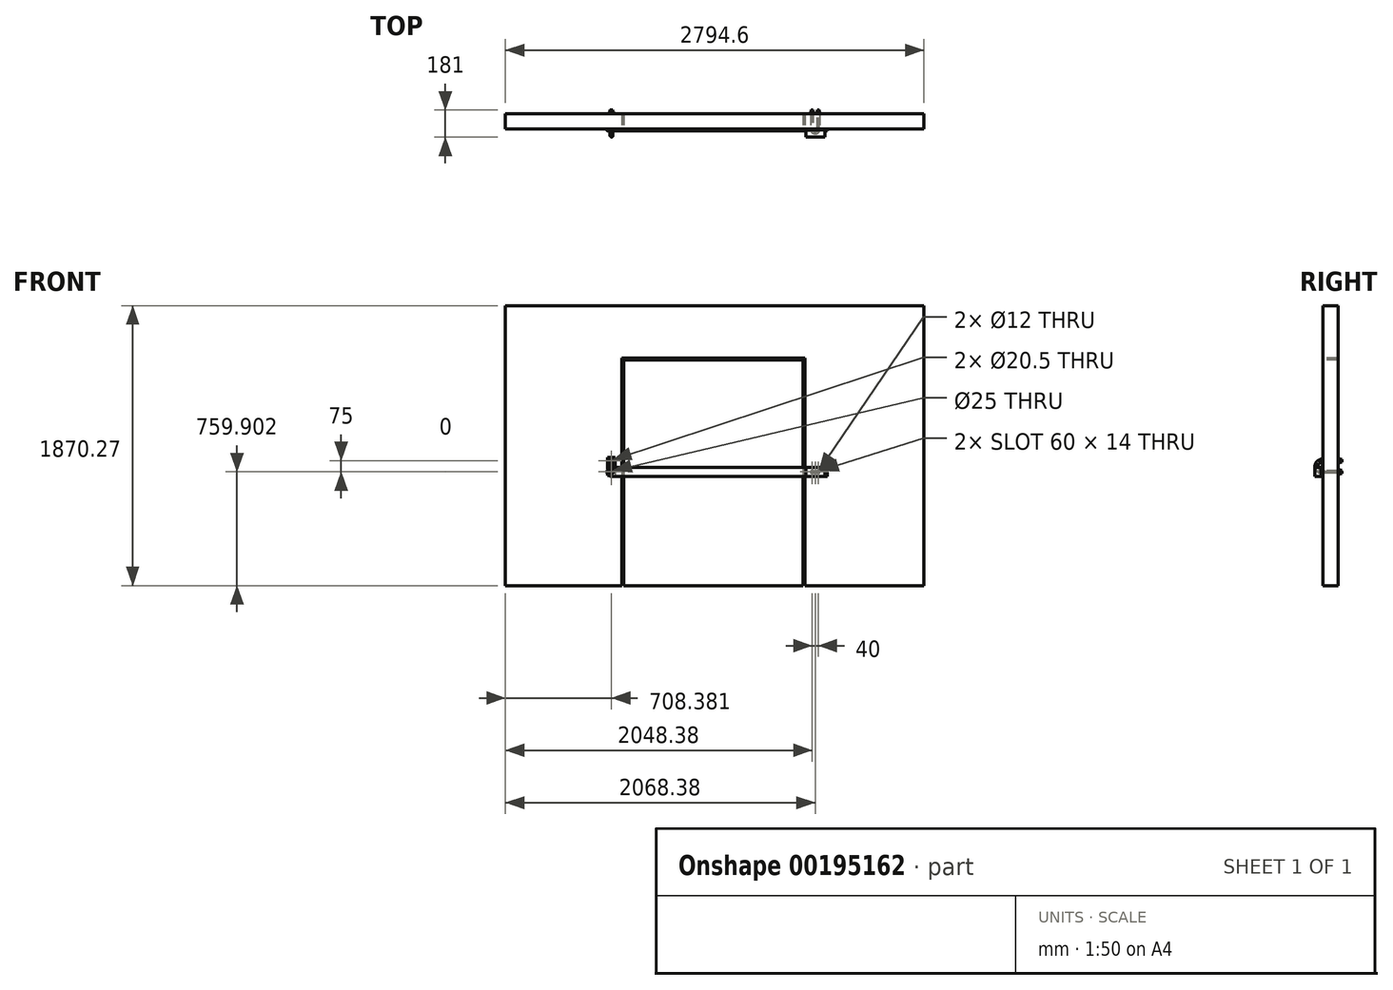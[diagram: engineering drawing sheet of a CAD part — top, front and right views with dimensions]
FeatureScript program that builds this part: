
annotation { "Feature Type Name" : "Feature", "Feature Type Description" : "" }
export const myFeature = defineFeature(function(context is Context, id is Id, definition is map)
    precondition{}
    {
        {
            assignVariable(context, id + "F0", {"name" : "LatchThickness", "anyValue" : 6});
        }
        {
            var Q0;
            Q0=qCreatedBy(makeId("Front.planeOp"),FACE);
            var sketch = newSketch(context, id + "F1", { "sketchPlane" : qUnion([Q0])});
            skLineSegment(sketch, "E0.bottom", {"start": v(-616.27, 618.17) * mm, "end": v(583.73, 618.17) * mm});
            skLineSegment(sketch, "E0.top", {"start": v(-616.27, -890.75) * mm, "end": v(583.73, -890.75) * mm});
            skLineSegment(sketch, "E0.left", {"start": v(-616.27, 618.17) * mm, "end": v(-616.27, -890.75) * mm});
            skLineSegment(sketch, "E0.right", {"start": v(583.73, 618.17) * mm, "end": v(583.73, -890.75) * mm});
            skLineSegment(sketch, "E1.bottom", {"start": v(-1404.65, 979.52) * mm, "end": v(-626.27, 979.52) * mm});
            skLineSegment(sketch, "E1.top", {"start": v(-1404.65, -890.75) * mm, "end": v(-626.27, -890.75) * mm});
            skLineSegment(sketch, "E1.left", {"start": v(-1404.65, 979.52) * mm, "end": v(-1404.65, -890.75) * mm});
            skLineSegment(sketch, "E1.right", {"start": v(-626.27, 628.17) * mm, "end": v(-626.27, -890.75) * mm});
            skLineSegment(sketch, "E2.bottom", {"start": v(-626.27, 979.52) * mm, "end": v(593.73, 979.52) * mm});
            skLineSegment(sketch, "E2.top", {"start": v(-626.27, 628.17) * mm, "end": v(593.73, 628.17) * mm});
            skLineSegment(sketch, "E3.bottom", {"start": v(593.73, 979.52) * mm, "end": v(1389.95, 979.52) * mm});
            skLineSegment(sketch, "E3.top", {"start": v(593.73, -890.75) * mm, "end": v(1389.95, -890.75) * mm});
            skLineSegment(sketch, "E3.left", {"start": v(593.73, 628.17) * mm, "end": v(593.73, -890.75) * mm});
            skLineSegment(sketch, "E3.right", {"start": v(1389.95, 979.52) * mm, "end": v(1389.95, -890.75) * mm});
            skSolve(sketch);
        }
        {
            var Q0;
            Q0 = qSketchRegion(id + "F1", true);
            extrude(context, id + "F2", {"entities" : qUnion([Q0]), "oppositeDirection" : true, "depth" : 100 * mm});
        }
        {
            var Q0;
            Q0=makeQuery(id+"F2.opExtrude","CAP_FACE",FACE,{"disambiguationData":[OSD([sQuery(id+"F1.wireOp",EDGE,"E1.bottom"),sQuery(id+"F1.wireOp",EDGE,"E1.top"),sQuery(id+"F1.wireOp",EDGE,"E1.left"),sQuery(id+"F1.wireOp",EDGE,"E1.right"),sQuery(id+"F1.wireOp",EDGE,"E2.bottom"),sQuery(id+"F1.wireOp",EDGE,"E2.top"),sQuery(id+"F1.wireOp",EDGE,"E3.bottom"),sQuery(id+"F1.wireOp",EDGE,"E3.top"),sQuery(id+"F1.wireOp",EDGE,"E3.left"),sQuery(id+"F1.wireOp",EDGE,"E3.right")])],"isStart":true});
            cPlane(context, id + "F3", {"entities" : qUnion([Q0]), "cplaneType" : CPlaneType.OFFSET, "offset" : 7 * mm, "width" : 150 * mm, "height" : 150 * mm});
        }
        {
            var Q0;
            Q0=qCreatedBy(id+"F3.planeOp",FACE);
            var sketch = newSketch(context, id + "F4", { "sketchPlane" : qUnion([Q0])});
            skLineSegment(sketch, "E4.bottom", {"start": v(-696.27, -100.85) * mm, "end": v(743.73, -100.85) * mm});
            skLineSegment(sketch, "E4.top", {"start": v(-696.27, -160.85) * mm, "end": v(743.73, -160.85) * mm});
            skLineSegment(sketch, "E4.left", {"start": v(-726.27, -130.85) * mm, "end": v(-726.27, -130.85) * mm});
            skLineSegment(sketch, "E4.right", {"start": v(743.73, -100.85) * mm, "end": v(743.73, -160.85) * mm});
            skPoint(sketch, "E5.visualSharp", {"position": v(-726.27, -100.85) * mm});
            skArc(sketch, "E5.filletArc", {"start": v(-696.27, -100.85) * mm, "mid": v(-717.48, -109.64) * mm, "end": v(-726.27, -130.85) * mm});
            skPoint(sketch, "E6.visualSharp", {"position": v(-726.27, -160.85) * mm});
            skArc(sketch, "E6.filletArc", {"start": v(-726.27, -130.85) * mm, "mid": v(-717.48, -152.06) * mm, "end": v(-696.27, -160.85) * mm});
            skCircle(sketch, "E7", {"center": v(-696.27, -130.85) * mm, "radius": 12.5 * mm});
            skSolve(sketch);
        }
        {
            var Q0;
            Q0 = qSketchRegion(id + "F4", true);
            extrude(context, id + "F5", {"entities" : qUnion([Q0]), "depth" : (getVariable(context, 'LatchThickness')) * mm});
        }
        {
            var Q0;
            Q0=makeQuery(id+"F2.opExtrude","SWEPT_FACE",FACE,{"disambiguationData":[OSD([sQuery(id+"F1.wireOp",EDGE,"E0.left")])]});
            cPlane(context, id + "F6", {"entities" : qUnion([Q0]), "cplaneType" : CPlaneType.OFFSET, "offset" : 80 * mm, "width" : 150 * mm, "height" : 150 * mm});
        }
        {
            var Q0;
            Q0=qCreatedBy(id+"F6.planeOp",FACE);
            var sketch = newSketch(context, id + "F7", { "sketchPlane" : qUnion([Q0])});
            skLineSegment(sketch, "E8.0", {"start": v(13, -100.85) * mm, "end": v(7, -100.85) * mm, "construction": true});
            skLineSegment(sketch, "E9.0", {"start": v(13, -160.85) * mm, "end": v(7, -160.85) * mm, "construction": true});
            skLineSegment(sketch, "E10.0", {"start": v(0, 979.52) * mm, "end": v(0, -890.75) * mm, "construction": true});
            skLineSegment(sketch, "E11", {"start": v(-125, -130.85) * mm, "end": v(7, -130.85) * mm});
            skLineSegment(sketch, "E12", {"start": v(7, -55.85) * mm, "end": v(-125, -55.85) * mm});
            skArc(sketch, "E13", {"start": v(7, -130.85) * mm, "mid": v(44.5, -93.35) * mm, "end": v(7, -55.85) * mm});
            skSolve(sketch);
        }
        {
            var Q0;
            Q0=sQuery(id+"F7.wireOp",EDGE,"E12");
            var Q1;
            Q1=sQuery(id+"F7.wireOp",VERTEX,"E12.end");
            cPlane(context, id + "F8", {"entities" : qUnion([Q0, Q1]), "cplaneType" : CPlaneType.CURVE_POINT, "offset" : 25 * mm, "width" : 150 * mm, "height" : 150 * mm});
        }
        {
            var Q0;
            Q0=qCreatedBy(id+"F8.planeOp",FACE);
            var sketch = newSketch(context, id + "F9", { "sketchPlane" : qUnion([Q0])});
            skCircle(sketch, "E14", {"center": v(696.27, -55.85) * mm, "radius": 10 * mm});
            skSolve(sketch);
        }
        {
            var Q0;
            Q0=makeQuery(id+"F9.imprint","IMPRINT",FACE,{"disambiguationData":[TD([[makeQuery(id+"F9.imprint","IMPRINT",EDGE,{"derivedFrom":sQuery(id+"F9.wireOp",EDGE,"E14")}),1.0]])]});
            var Q1;
            Q1=sQuery(id+"F7.wireOp",EDGE,"E12");
            var Q2;
            Q2=sQuery(id+"F7.wireOp",EDGE,"E13");
            var Q3;
            Q3=sQuery(id+"F7.wireOp",EDGE,"E11");
            sweep(context, id + "F10", {"profiles" : qUnion([Q0]), "path" : qUnion([Q1, Q2, Q3])});
        }
        {
            var Q0;
            Q0=makeQuery(id+"F2.opExtrude","CAP_FACE",FACE,{"disambiguationData":[OSD([sQuery(id+"F1.wireOp",EDGE,"E1.bottom"),sQuery(id+"F1.wireOp",EDGE,"E1.top"),sQuery(id+"F1.wireOp",EDGE,"E1.left"),sQuery(id+"F1.wireOp",EDGE,"E1.right"),sQuery(id+"F1.wireOp",EDGE,"E2.bottom"),sQuery(id+"F1.wireOp",EDGE,"E2.top"),sQuery(id+"F1.wireOp",EDGE,"E3.bottom"),sQuery(id+"F1.wireOp",EDGE,"E3.top"),sQuery(id+"F1.wireOp",EDGE,"E3.left"),sQuery(id+"F1.wireOp",EDGE,"E3.right")])],"isStart":true});
            var sketch = newSketch(context, id + "F11", { "sketchPlane" : qUnion([Q0])});
            skLineSegment(sketch, "E15.bottom", {"start": v(-721.27, -33.75) * mm, "end": v(-671.27, -33.75) * mm});
            skLineSegment(sketch, "E15.top", {"start": v(-721.27, -153.75) * mm, "end": v(-671.27, -153.75) * mm});
            skLineSegment(sketch, "E15.left", {"start": v(-721.27, -33.75) * mm, "end": v(-721.27, -153.75) * mm});
            skLineSegment(sketch, "E15.right", {"start": v(-671.27, -33.75) * mm, "end": v(-671.27, -153.75) * mm});
            skLineSegment(sketch, "E16", {"start": v(-706.27, -55.85) * mm, "end": v(-706.27, -130.85) * mm, "construction": true});
            skLineSegment(sketch, "E17", {"start": v(-686.27, -55.85) * mm, "end": v(-686.27, -130.85) * mm, "construction": true});
            skLineSegment(sketch, "E18", {"start": v(-696.27, 7.08) * mm, "end": v(-696.27, -206.8) * mm, "construction": true});
            skSolve(sketch);
        }
        {
            var Q0;
            Q0 = qSketchRegion(id + "F11", true);
            extrude(context, id + "F12", {"entities" : qUnion([Q0]), "operationType" : NewBodyOperationType.ADD, "depth" : 5 * mm});
        }
        {
            var Q0;
            Q0=makeQuery(id+"F2.opExtrude","CAP_FACE",FACE,{"disambiguationData":[OSD([sQuery(id+"F1.wireOp",EDGE,"E1.bottom"),sQuery(id+"F1.wireOp",EDGE,"E1.top"),sQuery(id+"F1.wireOp",EDGE,"E1.left"),sQuery(id+"F1.wireOp",EDGE,"E1.right"),sQuery(id+"F1.wireOp",EDGE,"E2.bottom"),sQuery(id+"F1.wireOp",EDGE,"E2.top"),sQuery(id+"F1.wireOp",EDGE,"E3.bottom"),sQuery(id+"F1.wireOp",EDGE,"E3.top"),sQuery(id+"F1.wireOp",EDGE,"E3.left"),sQuery(id+"F1.wireOp",EDGE,"E3.right")])],"isStart":false});
            var sketch = newSketch(context, id + "F13", { "sketchPlane" : qUnion([Q0])});
            skCircle(sketch, "E19", {"center": v(696.27, -55.85) * mm, "radius": 10.25 * mm});
            skCircle(sketch, "E20", {"center": v(696.27, -130.85) * mm, "radius": 10.25 * mm});
            skCircle(sketch, "E21", {"center": v(696.27, -55.85) * mm, "radius": 17.5 * mm});
            skCircle(sketch, "E22", {"center": v(696.27, -130.85) * mm, "radius": 17.5 * mm});
            skSolve(sketch);
        }
        {
            var Q0;
            Q0 = qSketchRegion(id + "F13", true);
            extrude(context, id + "F14", {"entities" : qUnion([Q0]), "depth" : 2 * mm});
        }
        {
            var Q0;
            Q0=makeQuery(id+"F14.opExtrude","CAP_FACE",FACE,{"disambiguationData":[OSD([sQuery(id+"F13.wireOp",EDGE,"E19"),sQuery(id+"F13.wireOp",EDGE,"E21")])],"isStart":false});
            var sketch = newSketch(context, id + "F15", { "sketchPlane" : qUnion([Q0])});
            skCircle(sketch, "E23.cCircle", {"center": v(696.27, -55.85) * mm, "radius": 12 * mm, "construction": true});
            skLineSegment(sketch, "E23.0", {"start": v(709.75, -59.04) * mm, "end": v(700.24, -69.12) * mm});
            skLineSegment(sketch, "E23.1", {"start": v(700.24, -69.12) * mm, "end": v(686.76, -65.93) * mm});
            skLineSegment(sketch, "E23.2", {"start": v(686.76, -65.93) * mm, "end": v(682.79, -52.65) * mm});
            skLineSegment(sketch, "E23.3", {"start": v(682.79, -52.65) * mm, "end": v(692.3, -42.57) * mm});
            skLineSegment(sketch, "E23.4", {"start": v(692.3, -42.57) * mm, "end": v(705.78, -45.77) * mm});
            skLineSegment(sketch, "E23.5", {"start": v(705.78, -45.77) * mm, "end": v(709.75, -59.04) * mm});
            skPoint(sketch, "E23.0.midPoint", {"position": v(705, -64.08) * mm});
            skCircle(sketch, "E24.cCircle", {"center": v(696.27, -130.85) * mm, "radius": 12 * mm, "construction": true});
            skLineSegment(sketch, "E24.0", {"start": v(709.75, -134.04) * mm, "end": v(700.24, -144.12) * mm});
            skLineSegment(sketch, "E24.1", {"start": v(700.24, -144.12) * mm, "end": v(686.76, -140.93) * mm});
            skLineSegment(sketch, "E24.2", {"start": v(686.76, -140.93) * mm, "end": v(682.79, -127.65) * mm});
            skLineSegment(sketch, "E24.3", {"start": v(682.79, -127.65) * mm, "end": v(692.3, -117.57) * mm});
            skLineSegment(sketch, "E24.4", {"start": v(692.3, -117.57) * mm, "end": v(705.78, -120.77) * mm});
            skLineSegment(sketch, "E24.5", {"start": v(705.78, -120.77) * mm, "end": v(709.75, -134.04) * mm});
            skPoint(sketch, "E24.0.midPoint", {"position": v(705, -139.08) * mm});
            skSolve(sketch);
        }
        {
            var Q0;
            Q0 = qSketchRegion(id + "F15", true);
            extrude(context, id + "F16", {"entities" : qUnion([Q0]), "depth" : 12 * mm});
        }
        {
            var Q0;
            Q0=makeQuery(id+"F5.opExtrude","CAP_FACE",FACE,{"disambiguationData":[OSD([sQuery(id+"F4.wireOp",EDGE,"E4.bottom"),sQuery(id+"F4.wireOp",EDGE,"E4.top"),sQuery(id+"F4.wireOp",EDGE,"E4.right"),sQuery(id+"F4.wireOp",EDGE,"E5.filletArc"),sQuery(id+"F4.wireOp",EDGE,"E6.filletArc"),sQuery(id+"F4.wireOp",EDGE,"E7")])],"isStart":false});
            var sketch = newSketch(context, id + "F17", { "sketchPlane" : qUnion([Q0])});
            skLineSegment(sketch, "E25.bottom", {"start": v(640.73, -123.85) * mm, "end": v(686.73, -123.85) * mm});
            skLineSegment(sketch, "E25.top", {"start": v(640.73, -137.85) * mm, "end": v(686.73, -137.85) * mm});
            skLineSegment(sketch, "E25.left", {"start": v(633.73, -130.85) * mm, "end": v(633.73, -130.85) * mm});
            skLineSegment(sketch, "E25.right", {"start": v(693.73, -130.85) * mm, "end": v(693.73, -130.85) * mm});
            skLineSegment(sketch, "E26", {"start": v(742.08, -130.85) * mm, "end": v(573.44, -130.85) * mm, "construction": true});
            skPoint(sketch, "E27.visualSharp", {"position": v(633.73, -123.85) * mm});
            skArc(sketch, "E27.filletArc", {"start": v(640.73, -123.85) * mm, "mid": v(635.78, -125.9) * mm, "end": v(633.73, -130.85) * mm});
            skPoint(sketch, "E28.visualSharp", {"position": v(633.73, -137.85) * mm});
            skArc(sketch, "E28.filletArc", {"start": v(633.73, -130.85) * mm, "mid": v(635.78, -135.8) * mm, "end": v(640.73, -137.85) * mm});
            skPoint(sketch, "E29.visualSharp", {"position": v(693.73, -123.85) * mm});
            skArc(sketch, "E29.filletArc", {"start": v(693.73, -130.85) * mm, "mid": v(691.68, -125.9) * mm, "end": v(686.73, -123.85) * mm});
            skPoint(sketch, "E30.visualSharp", {"position": v(693.73, -137.85) * mm});
            skArc(sketch, "E30.filletArc", {"start": v(686.73, -137.85) * mm, "mid": v(691.68, -135.8) * mm, "end": v(693.73, -130.85) * mm});
            skSolve(sketch);
        }
        {
            var Q0;
            Q0 = qSketchRegion(id + "F17", true);
            extrude(context, id + "F18", {"entities" : qUnion([Q0]), "operationType" : NewBodyOperationType.REMOVE, "endBound" : BoundingType.THROUGH_ALL, "oppositeDirection" : true, "depth" : 25 * mm});
        }
        {
            var Q0;
            Q0=makeQuery(id+"F5.opExtrude","SWEPT_FACE",FACE,{"disambiguationData":[OSD([sQuery(id+"F4.wireOp",EDGE,"E4.bottom")])]});
            var Q1;
            Q1=makeQuery(id+"F5.opExtrude","SWEPT_FACE",FACE,{"disambiguationData":[OSD([sQuery(id+"F4.wireOp",EDGE,"E4.top")])]});
            cPlane(context, id + "F19", {"entities" : qUnion([Q0, Q1]), "cplaneType" : CPlaneType.MID_PLANE, "offset" : 25 * mm, "width" : 150 * mm, "height" : 150 * mm});
        }
        {
            var Q0;
            Q0=qCreatedBy(id+"F19.planeOp",FACE);
            var sketch = newSketch(context, id + "F20", { "sketchPlane" : qUnion([Q0])});
            skPoint(sketch, "E31.0", {"position": v(633.73, -13) * mm});
            skPoint(sketch, "E32.0", {"position": v(693.73, -13) * mm});
            skLineSegment(sketch, "E33", {"start": v(643.73, -10) * mm, "end": v(643.73, 125) * mm});
            skLineSegment(sketch, "E34", {"start": v(683.73, 125) * mm, "end": v(683.73, -10) * mm});
            skArc(sketch, "E35", {"start": v(643.73, -10) * mm, "mid": v(663.73, -30) * mm, "end": v(683.73, -10) * mm});
            skLineSegment(sketch, "E36", {"start": v(663.73, 137.77) * mm, "end": v(663.73, -53.89) * mm, "construction": true});
            skSolve(sketch);
        }
        {
            var Q0;
            Q0=sQuery(id+"F20.wireOp",EDGE,"E33");
            var Q1;
            Q1=sQuery(id+"F20.wireOp",VERTEX,"E33.end");
            cPlane(context, id + "F21", {"entities" : qUnion([Q0, Q1]), "cplaneType" : CPlaneType.CURVE_POINT, "offset" : 25 * mm, "width" : 150 * mm, "height" : 150 * mm});
        }
        {
            var Q0;
            Q0=qCreatedBy(id+"F21.planeOp",FACE);
            var sketch = newSketch(context, id + "F22", { "sketchPlane" : qUnion([Q0])});
            skCircle(sketch, "E37", {"center": v(-643.73, -130.85) * mm, "radius": 6 * mm});
            skSolve(sketch);
        }
        {
            var Q0;
            Q0=makeQuery(id+"F22.imprint","IMPRINT",FACE,{"disambiguationData":[TD([[makeQuery(id+"F22.imprint","IMPRINT",EDGE,{"derivedFrom":sQuery(id+"F22.wireOp",EDGE,"E37")}),1.0]])]});
            var Q1;
            Q1=sQuery(id+"F20.wireOp",EDGE,"E33");
            var Q2;
            Q2=sQuery(id+"F20.wireOp",EDGE,"E35");
            var Q3;
            Q3=sQuery(id+"F20.wireOp",EDGE,"E34");
            sweep(context, id + "F23", {"profiles" : qUnion([Q0]), "path" : qUnion([Q1, Q2, Q3])});
        }
        {
            var Q0;
            Q0=makeQuery(id+"F2.opExtrude","CAP_FACE",FACE,{"disambiguationData":[OSD([sQuery(id+"F1.wireOp",EDGE,"E1.bottom"),sQuery(id+"F1.wireOp",EDGE,"E1.top"),sQuery(id+"F1.wireOp",EDGE,"E1.left"),sQuery(id+"F1.wireOp",EDGE,"E1.right"),sQuery(id+"F1.wireOp",EDGE,"E2.bottom"),sQuery(id+"F1.wireOp",EDGE,"E2.top"),sQuery(id+"F1.wireOp",EDGE,"E3.bottom"),sQuery(id+"F1.wireOp",EDGE,"E3.top"),sQuery(id+"F1.wireOp",EDGE,"E3.left"),sQuery(id+"F1.wireOp",EDGE,"E3.right")])],"isStart":false});
            var sketch = newSketch(context, id + "F24", { "sketchPlane" : qUnion([Q0])});
            skCircle(sketch, "E38", {"center": v(-643.73, -130.85) * mm, "radius": 6 * mm});
            skCircle(sketch, "E39", {"center": v(-643.73, -130.85) * mm, "radius": 10 * mm});
            skCircle(sketch, "E40", {"center": v(-683.73, -130.85) * mm, "radius": 6 * mm});
            skCircle(sketch, "E41", {"center": v(-683.73, -130.85) * mm, "radius": 10 * mm});
            skSolve(sketch);
        }
        {
            var Q0;
            Q0 = qSketchRegion(id + "F24", true);
            extrude(context, id + "F25", {"entities" : qUnion([Q0]), "depth" : 2 * mm});
        }
        {
            var Q0;
            Q0=makeQuery(id+"F25.opExtrude","CAP_FACE",FACE,{"disambiguationData":[OSD([sQuery(id+"F24.wireOp",EDGE,"E38"),sQuery(id+"F24.wireOp",EDGE,"E39")])],"isStart":false});
            var sketch = newSketch(context, id + "F26", { "sketchPlane" : qUnion([Q0])});
            skCircle(sketch, "E42.cCircle", {"center": v(-643.73, -130.85) * mm, "radius": 9.5 * mm, "construction": true});
            skLineSegment(sketch, "E42.0", {"start": v(-654.13, -127.37) * mm, "end": v(-645.92, -120.1) * mm});
            skLineSegment(sketch, "E42.1", {"start": v(-645.92, -120.1) * mm, "end": v(-635.51, -123.58) * mm});
            skLineSegment(sketch, "E42.2", {"start": v(-635.51, -123.58) * mm, "end": v(-633.33, -134.33) * mm});
            skLineSegment(sketch, "E42.3", {"start": v(-633.33, -134.33) * mm, "end": v(-641.55, -141.6) * mm});
            skLineSegment(sketch, "E42.4", {"start": v(-641.55, -141.6) * mm, "end": v(-651.95, -138.12) * mm});
            skLineSegment(sketch, "E42.5", {"start": v(-651.95, -138.12) * mm, "end": v(-654.13, -127.37) * mm});
            skPoint(sketch, "E42.0.midPoint", {"position": v(-650.02, -123.73) * mm});
            skCircle(sketch, "E43.cCircle", {"center": v(-683.73, -130.85) * mm, "radius": 9.5 * mm, "construction": true});
            skLineSegment(sketch, "E43.0", {"start": v(-693.6, -126.04) * mm, "end": v(-684.5, -119.9) * mm});
            skLineSegment(sketch, "E43.1", {"start": v(-684.5, -119.9) * mm, "end": v(-674.64, -124.71) * mm});
            skLineSegment(sketch, "E43.2", {"start": v(-674.64, -124.71) * mm, "end": v(-673.87, -135.65) * mm});
            skLineSegment(sketch, "E43.3", {"start": v(-673.87, -135.65) * mm, "end": v(-682.96, -141.8) * mm});
            skLineSegment(sketch, "E43.4", {"start": v(-682.96, -141.8) * mm, "end": v(-692.82, -136.99) * mm});
            skLineSegment(sketch, "E43.5", {"start": v(-692.82, -136.99) * mm, "end": v(-693.6, -126.04) * mm});
            skPoint(sketch, "E43.0.midPoint", {"position": v(-689.05, -122.97) * mm});
            skSolve(sketch);
        }
        {
            var Q0;
            Q0 = qSketchRegion(id + "F26", true);
            extrude(context, id + "F27", {"entities" : qUnion([Q0]), "depth" : 12 * mm});
        }
        {
            var Q0;
            Q0=makeQuery(id+"F5.opExtrude","CAP_FACE",FACE,{"disambiguationData":[OSD([sQuery(id+"F4.wireOp",EDGE,"E4.bottom"),sQuery(id+"F4.wireOp",EDGE,"E4.top"),sQuery(id+"F4.wireOp",EDGE,"E4.right"),sQuery(id+"F4.wireOp",EDGE,"E5.filletArc"),sQuery(id+"F4.wireOp",EDGE,"E6.filletArc"),sQuery(id+"F4.wireOp",EDGE,"E7")])],"isStart":false});
            var sketch = newSketch(context, id + "F28", { "sketchPlane" : qUnion([Q0])});
            skLineSegment(sketch, "E44", {"start": v(603.73, -160.85) * mm, "end": v(603.73, -103.85) * mm});
            skLineSegment(sketch, "E45", {"start": v(603.73, -103.85) * mm, "end": v(723.73, -103.85) * mm});
            skLineSegment(sketch, "E46", {"start": v(723.73, -103.85) * mm, "end": v(723.73, -160.85) * mm});
            skLineSegment(sketch, "E47", {"start": v(723.73, -160.85) * mm, "end": v(726.73, -160.85) * mm});
            skLineSegment(sketch, "E48", {"start": v(726.73, -160.85) * mm, "end": v(726.73, -100.85) * mm});
            skLineSegment(sketch, "E49", {"start": v(726.73, -100.85) * mm, "end": v(600.73, -100.85) * mm});
            skLineSegment(sketch, "E50", {"start": v(600.73, -100.85) * mm, "end": v(600.73, -160.85) * mm});
            skLineSegment(sketch, "E51", {"start": v(600.73, -160.85) * mm, "end": v(603.73, -160.85) * mm});
            skPoint(sketch, "E52.0", {"position": v(633.73, -130.85) * mm});
            skPoint(sketch, "E53.0", {"position": v(693.73, -130.85) * mm});
            skLineSegment(sketch, "E54", {"start": v(663.73, -77.58) * mm, "end": v(663.73, -186.08) * mm, "construction": true});
            skSolve(sketch);
        }
        {
            var Q0;
            Q0 = qSketchRegion(id + "F28", true);
            extrude(context, id + "F29", {"entities" : qUnion([Q0]), "operationType" : NewBodyOperationType.ADD, "depth" : 40 * mm});
        }
        {
            var Q0;
            Q0=makeQuery(id+"F29.opExtrude","CAP_FACE",FACE,{"disambiguationData":[OSD([sQuery(id+"F28.wireOp",EDGE,"E44"),sQuery(id+"F28.wireOp",EDGE,"E45"),sQuery(id+"F28.wireOp",EDGE,"E46"),sQuery(id+"F28.wireOp",EDGE,"E47"),sQuery(id+"F28.wireOp",EDGE,"E48"),sQuery(id+"F28.wireOp",EDGE,"E49"),sQuery(id+"F28.wireOp",EDGE,"E50"),sQuery(id+"F28.wireOp",EDGE,"E51")])],"isStart":false});
            var sketch = newSketch(context, id + "F30", { "sketchPlane" : qUnion([Q0])});
            skLineSegment(sketch, "E55.bottom", {"start": v(600.73, -100.85) * mm, "end": v(726.73, -100.85) * mm});
            skLineSegment(sketch, "E55.top", {"start": v(600.73, -160.85) * mm, "end": v(726.73, -160.85) * mm});
            skLineSegment(sketch, "E55.left", {"start": v(600.73, -100.85) * mm, "end": v(600.73, -160.85) * mm});
            skLineSegment(sketch, "E55.right", {"start": v(726.73, -100.85) * mm, "end": v(726.73, -160.85) * mm});
            skSolve(sketch);
        }
        {
            var Q0;
            Q0 = qSketchRegion(id + "F30", true);
            extrude(context, id + "F31", {"entities" : qUnion([Q0]), "operationType" : NewBodyOperationType.ADD, "depth" : 3 * mm});
        }
    });
